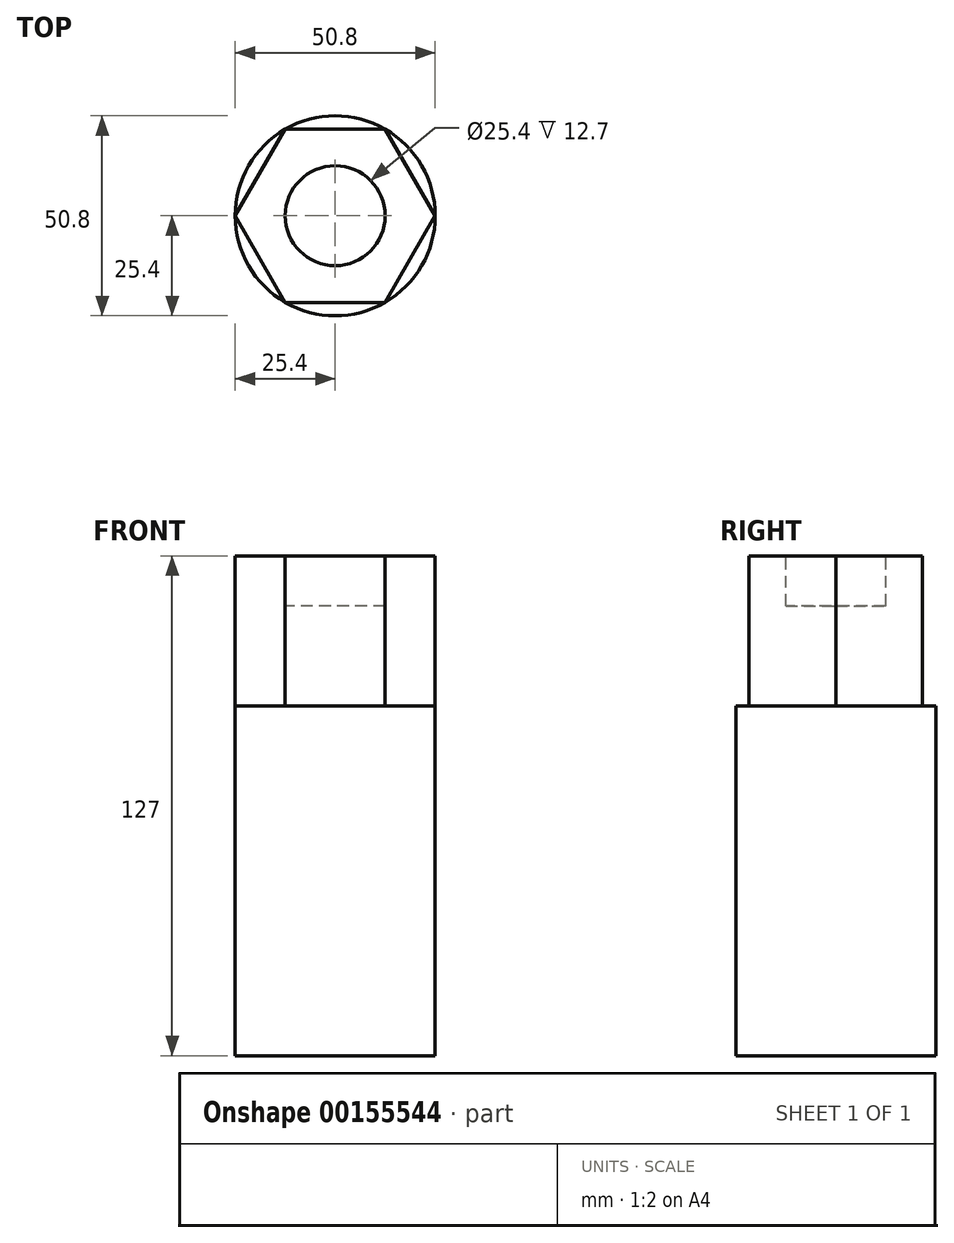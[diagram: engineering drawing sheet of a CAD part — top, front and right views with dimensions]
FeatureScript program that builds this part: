
annotation { "Feature Type Name" : "Feature", "Feature Type Description" : "" }
export const myFeature = defineFeature(function(context is Context, id is Id, definition is map)
    precondition{}
    {
        {
            var Q0;
            Q0=qCreatedBy(makeId("Top.planeOp"),FACE);
            var sketch = newSketch(context, id + "F0", { "sketchPlane" : qUnion([Q0])});
            skCircle(sketch, "E0", {"center": v(0, 0) * mm, "radius": 25.4 * mm});
            skSolve(sketch);
        }
        {
            var Q0;
            Q0=makeQuery(id+"F0.imprint","IMPRINT",FACE,{"disambiguationData":[TD([[makeQuery(id+"F0.imprint","IMPRINT",EDGE,{"derivedFrom":sQuery(id+"F0.wireOp",EDGE,"E0")}),1.0]])]});
            extrude(context, id + "F1", {"entities" : qUnion([Q0]), "depth" : 127 * mm});
        }
        {
            var Q0;
            Q0=makeQuery(id+"F1.opExtrude","CAP_FACE",FACE,{"disambiguationData":[OSD([sQuery(id+"F0.wireOp",EDGE,"E0")])],"isStart":false});
            var sketch = newSketch(context, id + "F2", { "sketchPlane" : qUnion([Q0])});
            skCircle(sketch, "E1.cCircle", {"center": v(0, 0) * mm, "radius": 25.4 * mm, "construction": true});
            skLineSegment(sketch, "E1.0", {"start": v(25.4, 0) * mm, "end": v(12.7, -22) * mm});
            skLineSegment(sketch, "E1.1", {"start": v(12.7, -22) * mm, "end": v(-12.7, -22) * mm});
            skLineSegment(sketch, "E1.2", {"start": v(-12.7, -22) * mm, "end": v(-25.4, 0) * mm});
            skLineSegment(sketch, "E1.3", {"start": v(-25.4, 0) * mm, "end": v(-12.7, 22) * mm});
            skLineSegment(sketch, "E1.4", {"start": v(-12.7, 22) * mm, "end": v(12.7, 22) * mm});
            skLineSegment(sketch, "E1.5", {"start": v(12.7, 22) * mm, "end": v(25.4, 0) * mm});
            skSolve(sketch);
        }
        {
            var Q0;
            {var subQ0=sQuery(id+"F2.wireOp",EDGE,"E1.2");Q0=makeQuery(id+"F2.imprint","IMPRINT",FACE,{"disambiguationData":[TD([[makeQuery(id+"F2.imprint","IMPRINT",EDGE,{"derivedFrom":subQ0}),1.0]])]});}
            var Q1;
            {var subQ0=sQuery(id+"F2.wireOp",EDGE,"E1.1");Q1=makeQuery(id+"F2.imprint","IMPRINT",FACE,{"disambiguationData":[TD([[makeQuery(id+"F2.imprint","IMPRINT",EDGE,{"derivedFrom":subQ0}),1.0]])]});}
            var Q2;
            {var subQ0=sQuery(id+"F2.wireOp",EDGE,"E1.0");Q2=makeQuery(id+"F2.imprint","IMPRINT",FACE,{"disambiguationData":[TD([[makeQuery(id+"F2.imprint","IMPRINT",EDGE,{"derivedFrom":subQ0}),1.0]])]});}
            var Q3;
            {var subQ0=sQuery(id+"F2.wireOp",EDGE,"E1.5");Q3=makeQuery(id+"F2.imprint","IMPRINT",FACE,{"disambiguationData":[TD([[makeQuery(id+"F2.imprint","IMPRINT",EDGE,{"derivedFrom":subQ0}),1.0]])]});}
            var Q4;
            {var subQ0=sQuery(id+"F2.wireOp",EDGE,"E1.4");Q4=makeQuery(id+"F2.imprint","IMPRINT",FACE,{"disambiguationData":[TD([[makeQuery(id+"F2.imprint","IMPRINT",EDGE,{"derivedFrom":subQ0}),1.0]])]});}
            var Q5;
            {var subQ0=sQuery(id+"F2.wireOp",EDGE,"E1.3");Q5=makeQuery(id+"F2.imprint","IMPRINT",FACE,{"disambiguationData":[TD([[makeQuery(id+"F2.imprint","IMPRINT",EDGE,{"derivedFrom":subQ0}),1.0]])]});}
            extrude(context, id + "F3", {"entities" : qUnion([Q0, Q1, Q2, Q3, Q4, Q5]), "operationType" : NewBodyOperationType.REMOVE, "oppositeDirection" : true, "depth" : 38.1 * mm});
        }
        {
            var Q0;
            Q0=makeQuery(id+"F1.opExtrude","CAP_FACE",FACE,{"disambiguationData":[OSD([sQuery(id+"F0.wireOp",EDGE,"E0")])],"isStart":false});
            var sketch = newSketch(context, id + "F4", { "sketchPlane" : qUnion([Q0])});
            skCircle(sketch, "E2", {"center": v(0, 0) * mm, "radius": 12.7 * mm});
            skSolve(sketch);
        }
        {
            var Q0;
            Q0 = qSketchRegion(id + "F4", true);
            extrude(context, id + "F5", {"entities" : qUnion([Q0]), "operationType" : NewBodyOperationType.REMOVE, "endBound" : BoundingType.SYMMETRIC, "oppositeDirection" : true, "depth" : 25.4 * mm});
        }
    });
